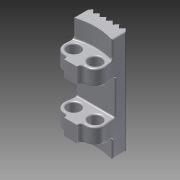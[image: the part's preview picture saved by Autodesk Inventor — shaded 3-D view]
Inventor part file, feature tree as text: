
AUTODESK INVENTOR PART (.ipt)
format: ipt  version: 2015 (Build 190159000, 159)  size: 721,408 bytes
history: native  units: mm
features: plane x7, sketch x6, extrude x6, projected_geometry x2, imported_body x1, hole x1, revolve x1, chamfer x1, fillet x1
ambient origin geometry x8: Origin, YZ Plane, XZ Plane, XY Plane, X Axis, Y Axis, Z Axis, Center Point
bodies: Body1 (feature_tree)
feature tree (26):
  plane  "Plano de trabajo1"
  plane  "Plano de trabajo2"
  imported_body  "Base"
  sketch  "Boceto5"  dims[d0=2.094395mm d1=2.094395mm d2=7.5mm d7=16.84218mm d16=3.75mm]
  plane  "Plano de trabajo9"
  extrude  "Extrusión7"  Depth=3.75mm
  extrude  "Extrusión8"  Depth=0.5mm
  sketch  "Boceto8"  dims[d17=7.5mm d18=0.5mm]
  sketch  "Boceto14"  dims[d19=1.5mm d20=2.5mm d21=7.5mm d22=0.5mm d23=1.0mm]
  hole  "Holes"  [1 undecoded]
  plane  "Plano de trabajo5"
  plane  "Plano de trabajo6"
  plane  "Plano de trabajo7"
  plane  "Plano de trabajo8"
  extrude  "Extrusión15"  Depth=15.0mm
  revolve  "Revolución3"  [1 undecoded]
  extrude  "Extrusión16"  [1 undecoded]
  sketch  "Boceto17"  dims[d29=8.0mm d30=0.5mm]
  extrude  "Extrusión17"  Depth=1.0mm
  sketch  "Boceto19"  dims[d36=8.25mm d37=-8.25mm d42=2.094395mm d43=2.094395mm d44=7.5mm d45=1.0mm d46=1.650539mm d47=10.821041mm d48=10.821041mm d49=1.0mm d50=4.18879mm d51=15.0mm d52=0.82527mm d53=21.642083mm d54=150.0mm d64=8.42109mm d67=0.2mm d71=8.62109mm d75=15.0mm d78=9.6mm d79=5.2mm d80=8.92109mm d81=2.5mm d82=6.75mm d83=5.2mm d84=5.618675mm d85=0.0mm d86=9.0mm d87=3.0mm d88=3.0mm d89=18.0mm d90=3.0mm d91=3.0mm d92=3.0mm d93=3.0mm d94=3.0mm d101=0.5mm d102=0.5mm d103=0.5mm d104=0.0mm d107=2.094395mm d108=2.094395mm d109=7.5mm d110=1.0mm d111=0.4mm d112=1.0mm d113=4.18879mm d114=15.0mm d115=150.0mm d124=4.18879mm d125=4.18879mm d126=1.8mm d127=1.0mm d133=0.1mm d134=4.0mm d135=1.5mm d136=-1.5mm d137=-4.0mm d149=4.8mm d154=1.0mm d156=2.094395mm d157=2.094395mm d158=7.5mm d159=1.0mm d160=0.4mm d161=4.18879mm d162=4.18879mm d163=1.8mm d164=1.0mm d165=1.8mm d166=1.0mm d167=4.18879mm d168=15.0mm d169=150.0mm d174=1.8mm d175=1.8mm d176=1.5mm d177=5.618675mm d178=15.0mm d179=0.0mm d180=90.0deg d181=4.0mm d182=4.0mm d183=0.2mm d184=9.6mm d185=2.5mm d186=1.0mm d187=16.0mm d188=5.0mm d189=5.0mm d190=10.0mm d191=18.0mm d192=0.0mm d193=8.92109mm d194=2.3mm d200=5.618675mm d201=0.468223mm d202=110.0mm d204=0.468223mm d205=10.0mm d207=10.0mm d209=20.0mm d210=0.0mm d216=0.8mm d217=0.0mm d219=2.8mm d220=2.8mm d221=5.0mm d222=0.8mm d223=2.0mm d224=45.0deg d225=0.6mm]
  extrude  "Extrusión19"  Depth=4.18879mm
  chamfer  "Chaflán1"  Distance=15.0mm
  fillet  "Empalme9"  Radius=0.82527mm
  sketch  "Boceto16"  dims[d24=1.0mm d25=15.0mm]
  projected_geometry  "Contorno proyectado3"
  projected_geometry  "Contorno proyectado4"
note: 3 required parameter values undecoded (feature->parameter linkage not recoverable at this tier; creation-order binding heuristic only, values carry confidence <= 0.55)